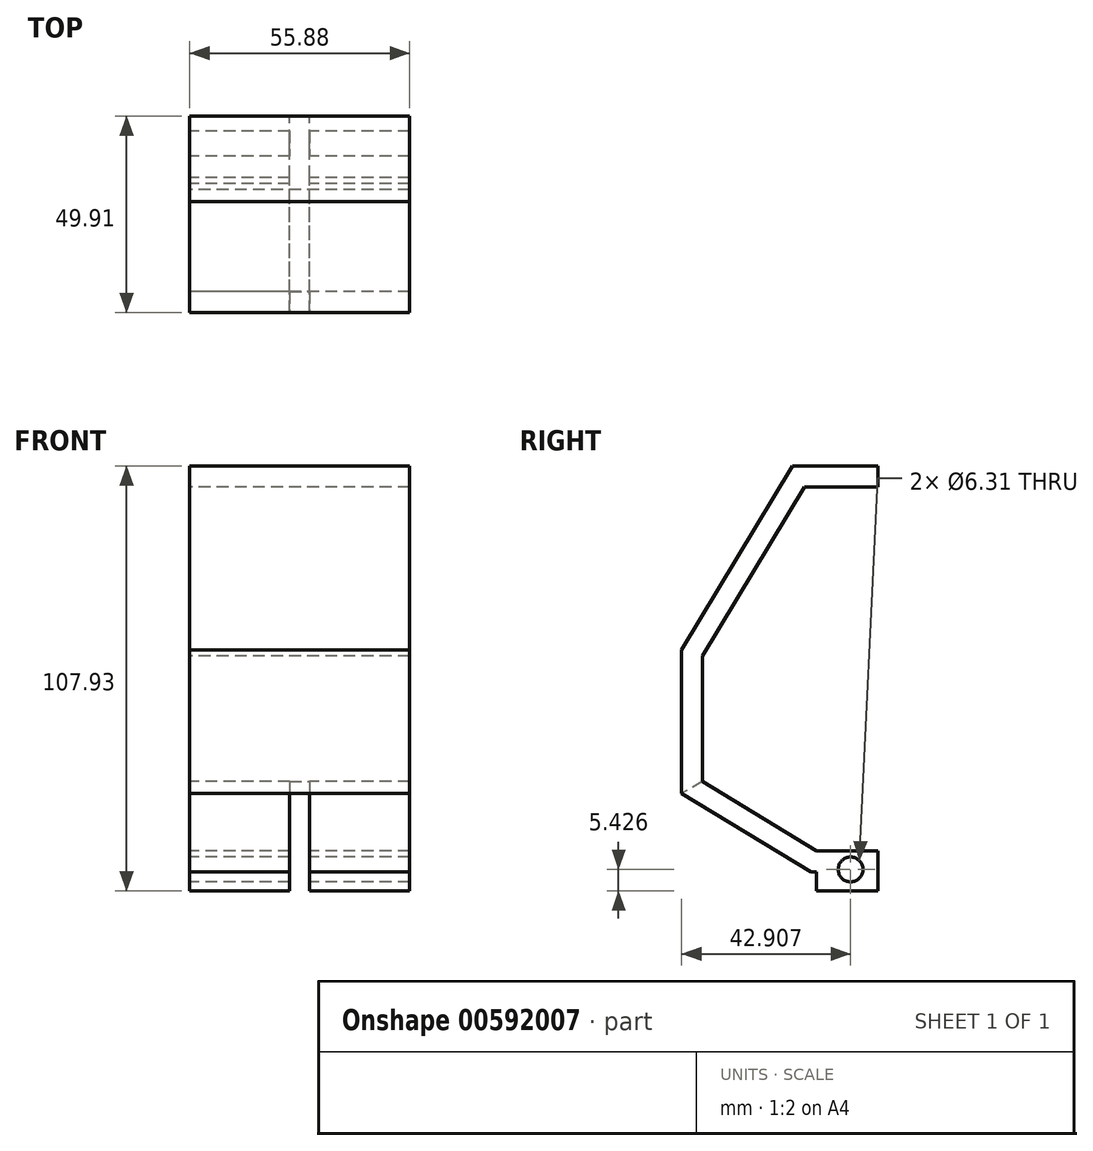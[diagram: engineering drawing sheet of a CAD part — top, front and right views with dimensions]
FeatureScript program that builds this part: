
annotation { "Feature Type Name" : "Feature", "Feature Type Description" : "" }
export const myFeature = defineFeature(function(context is Context, id is Id, definition is map)
    precondition{}
    {
        {
            var Q0;
            Q0=qCreatedBy(makeId("Right.planeOp"),FACE);
            var sketch = newSketch(context, id + "F0", { "sketchPlane" : qUnion([Q0])});
            skLineSegment(sketch, "E0", {"start": v(0, 58.7) * mm, "end": v(-21.71, 58.7) * mm});
            skLineSegment(sketch, "E1", {"start": v(-21.71, 58.7) * mm, "end": v(-49.91, 11.91) * mm});
            skLineSegment(sketch, "E2", {"start": v(-49.91, 11.91) * mm, "end": v(-49.91, -24.44) * mm});
            skLineSegment(sketch, "E3", {"start": v(-49.91, -24.44) * mm, "end": v(-17.13, -44.4) * mm});
            skLineSegment(sketch, "E4", {"start": v(-17.13, -44.4) * mm, "end": v(0, -44.4) * mm});
            skLineSegment(sketch, "E5.0", {"start": v(-15.64, -39.07) * mm, "end": v(0, -39.07) * mm});
            skLineSegment(sketch, "E5.1", {"start": v(0, 53.37) * mm, "end": v(-18.7, 53.37) * mm});
            skLineSegment(sketch, "E5.2", {"start": v(-18.7, 53.37) * mm, "end": v(-44.58, 10.43) * mm});
            skLineSegment(sketch, "E5.3", {"start": v(-44.58, 10.43) * mm, "end": v(-44.58, -21.44) * mm});
            skLineSegment(sketch, "E5.4", {"start": v(-44.58, -21.44) * mm, "end": v(-15.64, -39.07) * mm});
            skLineSegment(sketch, "E6", {"start": v(0, 58.7) * mm, "end": v(0, 53.37) * mm});
            skLineSegment(sketch, "E7", {"start": v(0, -39.07) * mm, "end": v(0, -44.4) * mm});
            skLineSegment(sketch, "E8", {"start": v(-44.58, -21.44) * mm, "end": v(-49.91, -24.44) * mm});
            skSolve(sketch);
        }
        {
            var Q0;
            Q0 = qSketchRegion(id + "F0", true);
            extrude(context, id + "F1", {"entities" : qUnion([Q0]), "depth" : 25.4 * mm, "offsetDistance" : 25.4 * mm});
        }
        {
            var Q0;
            Q0=makeQuery(id+"F1.opExtrude","SWEPT_FACE",FACE,{"disambiguationData":[OSD([sQuery(id+"F0.wireOp",EDGE,"E5.0")])]});
            extrude(context, id + "F2", {"entities" : qUnion([Q0]), "operationType" : NewBodyOperationType.ADD, "oppositeDirection" : true, "depth" : 10.16 * mm, "offsetDistance" : 25.4 * mm});
        }
        {
            var Q0;
            {var subQ0=sQuery(id+"F0.wireOp",EDGE,"E5.0");Q0=makeQuery(id+"F2.boolean.opBoolean","MERGE",FACE,{"derivedFrom":[makeQuery(id+"F1.opExtrude","CAP_FACE",FACE,{"disambiguationData":[OSD([sQuery(id+"F0.wireOp",EDGE,"E0"),sQuery(id+"F0.wireOp",EDGE,"E1"),sQuery(id+"F0.wireOp",EDGE,"E2"),sQuery(id+"F0.wireOp",EDGE,"E3"),sQuery(id+"F0.wireOp",EDGE,"E4"),subQ0,sQuery(id+"F0.wireOp",EDGE,"E5.1"),sQuery(id+"F0.wireOp",EDGE,"E5.2"),sQuery(id+"F0.wireOp",EDGE,"E5.3"),sQuery(id+"F0.wireOp",EDGE,"E5.4"),sQuery(id+"F0.wireOp",EDGE,"E6"),sQuery(id+"F0.wireOp",EDGE,"E7")])],"isStart":true}),makeQuery(id+"F2.opExtrude","SWEPT_FACE",FACE,{"disambiguationData":[OSD([subQ0]),TDD([makeQuery(id+"F1.opExtrude","CAP_EDGE",EDGE,{"disambiguationData":[OSD([subQ0])],"isStart":true})])]})]});}
            var sketch = newSketch(context, id + "F3", { "sketchPlane" : qUnion([Q0])});
            skCircle(sketch, "E9", {"center": v(7, -43.8) * mm, "radius": 3.15 * mm});
            skSolve(sketch);
        }
        {
            var Q0;
            Q0=makeQuery(id+"F3.imprint","IMPRINT",FACE,{"disambiguationData":[TD([[makeQuery(id+"F3.imprint","IMPRINT",EDGE,{"derivedFrom":sQuery(id+"F3.wireOp",EDGE,"E9")}),1.0]])]});
            extrude(context, id + "F4", {"entities" : qUnion([Q0]), "operationType" : NewBodyOperationType.REMOVE, "oppositeDirection" : true, "depth" : 25.4 * mm, "offsetDistance" : 25.4 * mm});
        }
        {
            var Q0;
            {var subQ0=sQuery(id+"F0.wireOp",EDGE,"E5.0");Q0=makeQuery(id+"F2.boolean.opBoolean","MERGE",FACE,{"derivedFrom":[makeQuery(id+"F1.opExtrude","CAP_FACE",FACE,{"disambiguationData":[OSD([sQuery(id+"F0.wireOp",EDGE,"E0"),sQuery(id+"F0.wireOp",EDGE,"E1"),sQuery(id+"F0.wireOp",EDGE,"E2"),sQuery(id+"F0.wireOp",EDGE,"E3"),sQuery(id+"F0.wireOp",EDGE,"E4"),subQ0,sQuery(id+"F0.wireOp",EDGE,"E5.1"),sQuery(id+"F0.wireOp",EDGE,"E5.2"),sQuery(id+"F0.wireOp",EDGE,"E5.3"),sQuery(id+"F0.wireOp",EDGE,"E5.4"),sQuery(id+"F0.wireOp",EDGE,"E6"),sQuery(id+"F0.wireOp",EDGE,"E7")])],"isStart":true}),makeQuery(id+"F2.opExtrude","SWEPT_FACE",FACE,{"disambiguationData":[OSD([subQ0]),TDD([makeQuery(id+"F1.opExtrude","CAP_EDGE",EDGE,{"disambiguationData":[OSD([subQ0])],"isStart":true})])]})]});}
            extrude(context, id + "F5", {"entities" : qUnion([Q0]), "operationType" : NewBodyOperationType.ADD, "depth" : 30.48 * mm, "offsetDistance" : 25.4 * mm});
        }
        {
            var Q0;
            Q0=makeQuery(id+"F3.imprint","IMPRINT",FACE,{"disambiguationData":[TD([[makeQuery(id+"F3.imprint","IMPRINT",EDGE,{"derivedFrom":sQuery(id+"F3.wireOp",EDGE,"E9")}),-1.0]])]});
            extrude(context, id + "F6", {"entities" : qUnion([Q0]), "operationType" : NewBodyOperationType.REMOVE, "depth" : 5.08 * mm, "offsetDistance" : 25.4 * mm});
        }
        {
            var Q0;
            Q0=makeQuery(id+"F0.imprint","IMPRINT",FACE,{"disambiguationData":[TD([[makeQuery(id+"F0.imprint","IMPRINT",EDGE,{"derivedFrom":sQuery(id+"F0.wireOp",EDGE,"E0")}),1.0]])]});
            extrude(context, id + "F7", {"entities" : qUnion([Q0]), "operationType" : NewBodyOperationType.ADD, "oppositeDirection" : true, "depth" : 5.08 * mm, "offsetDistance" : 25.4 * mm});
        }
    });
